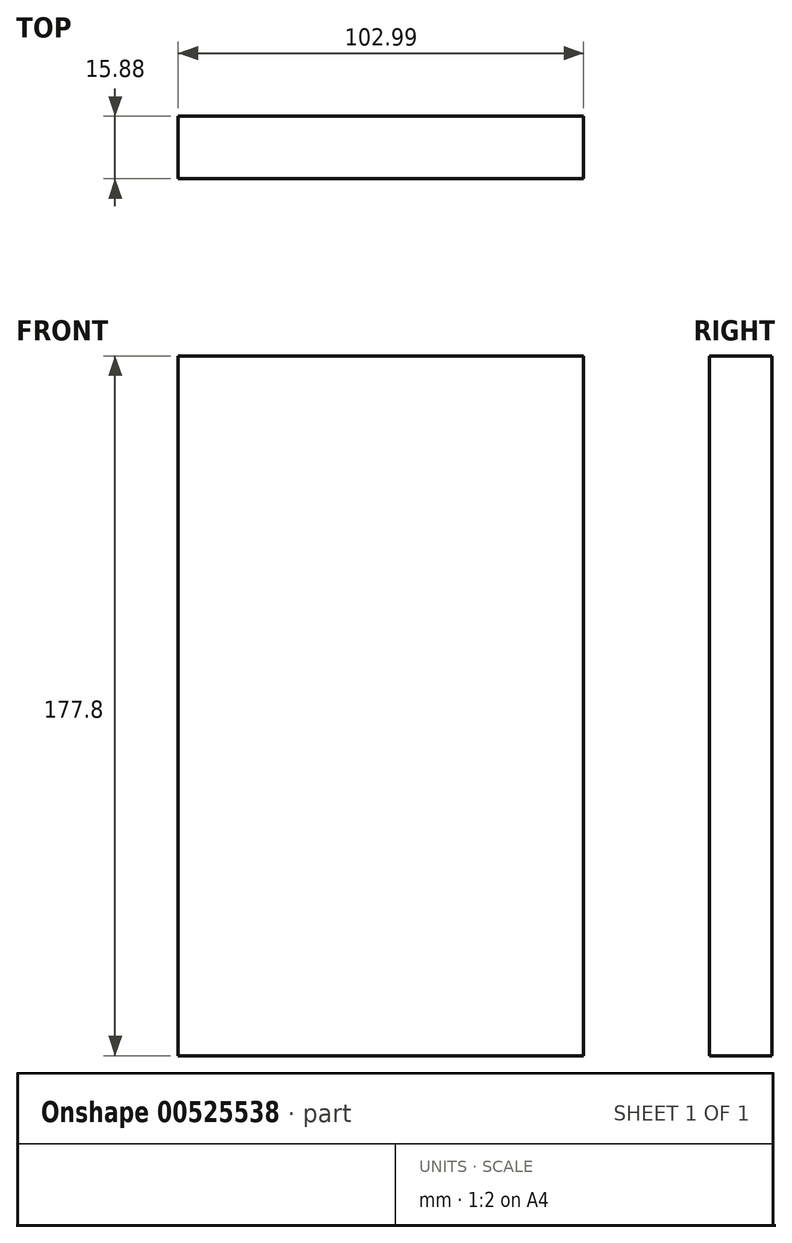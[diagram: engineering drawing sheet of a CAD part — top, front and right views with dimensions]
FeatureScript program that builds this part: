
annotation { "Feature Type Name" : "Feature", "Feature Type Description" : "" }
export const myFeature = defineFeature(function(context is Context, id is Id, definition is map)
    precondition{}
    {
        {
            var Q0;
            Q0=qCreatedBy(makeId("Front.planeOp"),FACE);
            var sketch = newSketch(context, id + "F0", { "sketchPlane" : qUnion([Q0])});
            skLineSegment(sketch, "E0.bottom", {"start": v(-52.22, 91.55) * mm, "end": v(50.77, 91.55) * mm});
            skLineSegment(sketch, "E0.top", {"start": v(-52.22, -86.25) * mm, "end": v(50.77, -86.25) * mm});
            skLineSegment(sketch, "E0.left", {"start": v(-52.22, 91.55) * mm, "end": v(-52.22, -86.25) * mm});
            skLineSegment(sketch, "E0.right", {"start": v(50.77, 91.55) * mm, "end": v(50.77, -86.25) * mm});
            skSolve(sketch);
        }
        {
            var Q0;
            Q0 = qSketchRegion(id + "F0", true);
            extrude(context, id + "F1", {"entities" : qUnion([Q0]), "depth" : 15.88 * mm, "offsetDistance" : 25.4 * mm});
        }
    });
